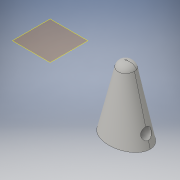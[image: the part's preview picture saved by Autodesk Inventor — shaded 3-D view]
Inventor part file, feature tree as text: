
AUTODESK INVENTOR PART (.ipt)
format: ipt  version: 2016 (Build 200138000, 138)  size: 228,864 bytes
history: native  units: in
note: dims shown in document units (in); Inventor stores cm internally (conversion verified against a paired STEP export)
features: sketch x3, plane x1, loft x1, fillet x1, extrude x1
ambient origin geometry x8: Origin, YZ Plane, XZ Plane, XY Plane, X Axis, Y Axis, Z Axis, Center Point
bodies: Body1 (feature_tree)
feature tree (7):
  sketch  "Sketch1"  dims[d0=0.3937in d1=0.5512in d13=0.315in]
  plane  "Work Plane4"
  loft  "Loft2"
  fillet  "Fillet3"  Radius=0.315in
  extrude  "Extrusion2"  TaperAngle=0.0deg  [1 undecoded]
  sketch  "Sketch8"  dims[d14=0.0in d15=90.0deg d16=0.0in d17=90.0deg]
  sketch  "Sketch9"  dims[d19=0.1689in d20=0.2362in d21=0.2756in d22=0.1969in d23=0.0in]
note: 1 required parameter value undecoded (feature->parameter linkage not recoverable at this tier; creation-order binding heuristic only, values carry confidence <= 0.55)
